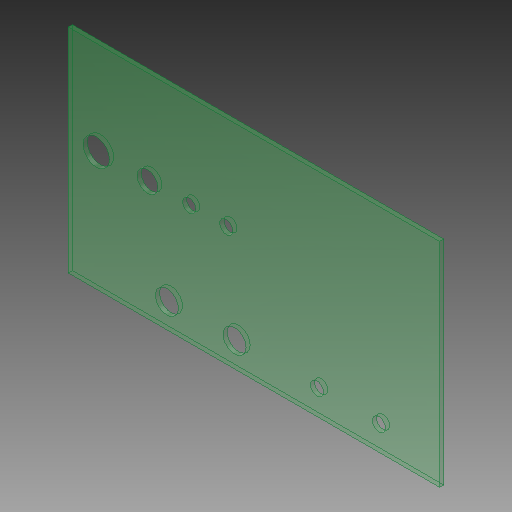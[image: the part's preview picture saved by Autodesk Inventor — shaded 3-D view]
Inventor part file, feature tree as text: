
AUTODESK INVENTOR PART (.ipt)
format: ipt  version: 2018.1 (Build 221171000, 171)  size: 148,992 bytes
history: native  units: mm
features: extrude x2, sketch x2
ambient origin geometry x8: Origin, YZ Plane, XZ Plane, XY Plane, X Axis, Y Axis, Z Axis, Center Point
bodies: Solid1 (feature_tree)
feature tree (4):
  extrude  "Extrusion1"  Depth=258.0mm
  extrude  "Extrusion2"  TaperAngle=0.0deg  [1 undecoded]
  sketch  "Sketch1"  dims[d0=450.0mm d1=258.0mm]
  sketch  "Sketch2"  dims[d2=5.0mm d3=0.0mm d4=39.0mm d5=29.5mm d6=119.5mm d7=39.0mm d8=25.0mm d9=25.0mm d10=48.0mm d11=36.0mm d12=25.0mm d13=25.0mm d14=29.5mm d15=29.5mm d16=29.5mm d17=144.0mm d18=144.0mm d19=144.0mm d20=144.0mm d21=82.0mm d22=100.0mm d23=75.0mm d24=34.0mm d25=62.0mm d26=50.5mm d27=45.0mm d28=32.0mm d29=25.0mm d30=16.0mm d31=16.0mm d32=28.0mm d33=28.0mm d34=16.0mm d35=16.0mm d36=5.0mm d37=0.0mm]
note: 1 required parameter value undecoded (feature->parameter linkage not recoverable at this tier; creation-order binding heuristic only, values carry confidence <= 0.55)
